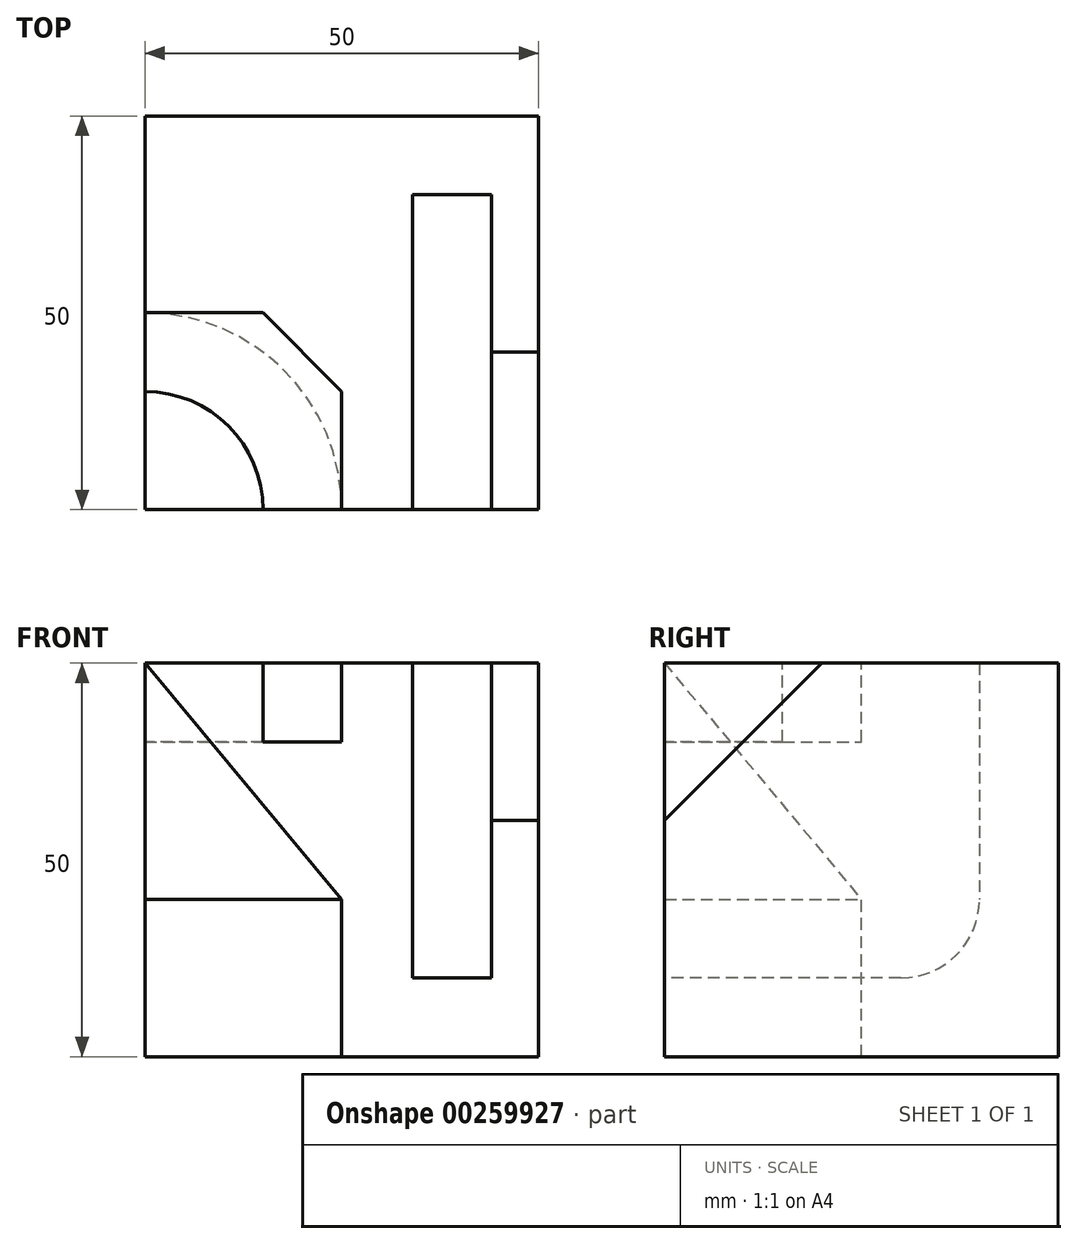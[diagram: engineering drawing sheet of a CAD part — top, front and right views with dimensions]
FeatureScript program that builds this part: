
annotation { "Feature Type Name" : "Feature", "Feature Type Description" : "" }
export const myFeature = defineFeature(function(context is Context, id is Id, definition is map)
    precondition{}
    {
        {
            var Q0;
            Q0=qCreatedBy(makeId("Top.planeOp"),FACE);
            var sketch = newSketch(context, id + "F0", { "sketchPlane" : qUnion([Q0])});
            skLineSegment(sketch, "E0.bottom", {"start": v(0, 0) * mm, "end": v(50, 0) * mm});
            skLineSegment(sketch, "E0.top", {"start": v(0, 50) * mm, "end": v(50, 50) * mm});
            skLineSegment(sketch, "E0.left", {"start": v(0, 0) * mm, "end": v(0, 50) * mm});
            skLineSegment(sketch, "E0.right", {"start": v(50, 0) * mm, "end": v(50, 50) * mm});
            skSolve(sketch);
        }
        {
            var Q0;
            Q0 = qSketchRegion(id + "F0", true);
            extrude(context, id + "F1", {"entities" : qUnion([Q0]), "depth" : 50 * mm});
        }
        {
            var Q0;
            Q0=makeQuery(id+"F1.opExtrude","SWEPT_FACE",FACE,{"disambiguationData":[OSD([sQuery(id+"F0.wireOp",EDGE,"E0.bottom")])]});
            var sketch = newSketch(context, id + "F2", { "sketchPlane" : qUnion([Q0])});
            skLineSegment(sketch, "E1.bottom", {"start": v(44, 50) * mm, "end": v(34, 50) * mm});
            skLineSegment(sketch, "E1.top", {"start": v(44, 10) * mm, "end": v(34, 10) * mm});
            skLineSegment(sketch, "E1.left", {"start": v(44, 50) * mm, "end": v(44, 10) * mm});
            skLineSegment(sketch, "E1.right", {"start": v(34, 50) * mm, "end": v(34, 10) * mm});
            skSolve(sketch);
        }
        {
            var Q0;
            Q0 = qSketchRegion(id + "F2", true);
            extrude(context, id + "F3", {"entities" : qUnion([Q0]), "operationType" : NewBodyOperationType.REMOVE, "oppositeDirection" : true, "depth" : 40 * mm});
        }
        {
            var Q0;
            Q0=makeQuery(id+"F3.boolean.opBoolean","COPY",EDGE,{"derivedFrom":makeQuery(id+"F3.opExtrude","CAP_EDGE",EDGE,{"disambiguationData":[OSD([sQuery(id+"F2.wireOp",EDGE,"E1.top")])],"isStart":false})});
            fillet(context, id + "F4", {"entities" : qUnion([Q0]), "radius" : 10 * mm, "tangentPropagation" : true, "allowEdgeOverflow" : false});
        }
        {
            var Q0;
            Q0=makeQuery(id+"F1.opExtrude","SWEPT_FACE",FACE,{"disambiguationData":[OSD([sQuery(id+"F0.wireOp",EDGE,"E0.bottom")])]});
            var sketch = newSketch(context, id + "F5", { "sketchPlane" : qUnion([Q0])});
            skLineSegment(sketch, "E2", {"start": v(0, 50) * mm, "end": v(25, 20) * mm});
            skLineSegment(sketch, "E3", {"start": v(25, 20) * mm, "end": v(25, 0) * mm});
            skLineSegment(sketch, "E4", {"start": v(25, 0) * mm, "end": v(0, 0) * mm});
            skLineSegment(sketch, "E5", {"start": v(0, 0) * mm, "end": v(0, 50) * mm});
            skSolve(sketch);
        }
        {
            var Q0;
            Q0 = qSketchRegion(id + "F5", true);
            var Q1;
            Q1=sQuery(id+"F5.wireOp",EDGE,"E5");
            revolve(context, id + "F6", {"operationType" : NewBodyOperationType.REMOVE, "entities" : qUnion([Q0]), "axis" : qUnion([Q1]), "revolveType" : RevolveType.FULL, "oppositeDirection" : true});
        }
        {
            var Q0;
            Q0=makeQuery(id+"F1.opExtrude","CAP_FACE",FACE,{"disambiguationData":[OSD([sQuery(id+"F0.wireOp",EDGE,"E0.bottom"),sQuery(id+"F0.wireOp",EDGE,"E0.top"),sQuery(id+"F0.wireOp",EDGE,"E0.left"),sQuery(id+"F0.wireOp",EDGE,"E0.right")])],"isStart":false});
            var sketch = newSketch(context, id + "F7", { "sketchPlane" : qUnion([Q0])});
            skArc(sketch, "E6", {"start": v(15, 0) * mm, "mid": v(10.6, 10.6) * mm, "end": v(0, 15) * mm});
            skLineSegment(sketch, "E7", {"start": v(0, 15) * mm, "end": v(0, 25) * mm});
            skLineSegment(sketch, "E8", {"start": v(0, 25) * mm, "end": v(25, 25) * mm});
            skLineSegment(sketch, "E9", {"start": v(25, 25) * mm, "end": v(25, 0) * mm});
            skLineSegment(sketch, "E10", {"start": v(25, 0) * mm, "end": v(15, 0) * mm});
            skSolve(sketch);
        }
        {
            var Q0;
            Q0=makeQuery(id+"F7.imprint","IMPRINT",FACE,{"disambiguationData":[TD([[makeQuery(id+"F7.imprint","IMPRINT",EDGE,{"derivedFrom":sQuery(id+"F7.wireOp",EDGE,"E6")}),-1.0]])]});
            extrude(context, id + "F8", {"entities" : qUnion([Q0]), "operationType" : NewBodyOperationType.REMOVE, "oppositeDirection" : true, "depth" : 10 * mm});
        }
        {
            var Q0;
            Q0=makeQuery(id+"F8.boolean.opBoolean","COPY",EDGE,{"derivedFrom":makeQuery(id+"F8.opExtrude","SWEPT_EDGE",EDGE,{"disambiguationData":[OSD([sQuery(id+"F7.wireOp",EDGE,"E8"),sQuery(id+"F7.wireOp",EDGE,"E9")])]})});
            chamfer(context, id + "F9", {"entities" : qUnion([Q0]), "width" : 10 * mm, "tangentPropagation" : true});
        }
        {
            var Q0;
            {var subQ0=sQuery(id+"F0.wireOp",EDGE,"E0.bottom");var subQ1=sQuery(id+"F0.wireOp",EDGE,"E0.right");Q0=makeQuery(id+"F3.boolean.opBoolean","SPLIT",EDGE,{"disambiguationData":[TD([makeQuery(id+"F1.opExtrude","SWEPT_FACE",FACE,{"disambiguationData":[OSD([subQ1])]})])],"derivedFrom":makeQuery(id+"F1.opExtrude","CAP_EDGE",EDGE,{"disambiguationData":[OSD([subQ0])],"isStart":false})});}
            chamfer(context, id + "F10", {"entities" : qUnion([Q0]), "width" : 20 * mm, "tangentPropagation" : true});
        }
    });
